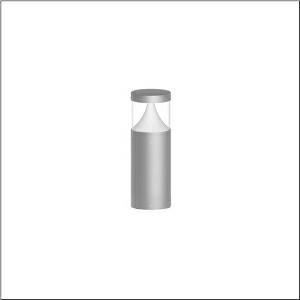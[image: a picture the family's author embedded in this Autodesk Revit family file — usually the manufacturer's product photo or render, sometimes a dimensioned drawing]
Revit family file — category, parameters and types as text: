
# Revit family: cl_31_poller_40_5cl424603
name_source: partatom
category: Lighting Fixtures
units: mm (PartAtom-declared; Revit-internal decimal feet)

## family parameters
Cut with Voids When Loaded = No
Host = Face
Light Source = No
Part Type = Normal
Room Calculation Point = No
Round Connector Dimension = Use Diameter
Shared = No

## types (1)
- --- (1 x LED, 800 lm, 7.2 W, 3000K)
    Apparent Load = 7 VA
    CIE Flux Codes = 19 66 88 92 100
    Color Rendering = 80
    Color Temperature = 3000K
    Default Elevation = 1800 mm
    Description = CL 31 Bollard 40, bollard luminaire, primary light control with lens, of PC, primary optical cover: cover panel, of PC, transparent, secondary light control with reflector, of PC, primary light characteristic: asymmetric, LED, rated luminous flux: 800lm, luminous efficacy: 110lm/W, light colour: 830, colour temperature: 3000K, control gear: DALI, with terminal, 5-pole, max. 2.5mm², mains connection: 220..240V, AC, 50/60Hz, rated input power: 7.2W, luminaire housing, of aluminium, powder-coated, Siteco® metallic grey, diameter: 170mm, height: 400mm, protection rating (complete): IP65, insulation class (complete): insulation class I (protective earthing), certification: CE, ENEC, impact resistance: IK10, permissible operating ambient temperature for outdoor applications: -20..+50°C, packaging unit: 1 piece
    Height = 200 mm  [stored 0.656168 ft]
    Lamp = 1 x LED
    Lamp Light Flux = 800 lm
    Lamp Power = 7.2 W
    Lamp count = 1
    Length = 170 mm  [stored 0.557743 ft]
    Luminous efficacy = 111 lm/W
    Manufacturer = Siteco
    ModVariant = No
    Model = 5CL424603
    Mounting Place = Floor
    Mounting Type = Freestanding
    Number of Poles = 1
    OnlyDefault = Yes
    Power Factor = 1
    Product Name = CL 31 Poller 40
    Product group = bollard luminaire
    ProductGroupID = 1304
    Protection Class = Protection class I
    Protection Degree = IP 65
    RLX_Detail_Level = 1
    RLX_Emergency_Light_Flux = 0 lm
    RLX_Emergency_Type = 0
    RLX_Emergency_Type_DB = No
    RlxData = <blob elided: 62325 chars, md5=652fc642>
    Socket = socket
    Standby Power = 0 W
    System Light Flux = 800 lm
    System Power = 7 W
    Type Comments = factory setting: luminous flux: 100 % | dim-lin: 254 | 182 mA
    Type Image = l_1006907.jpg
    URL = http://relux.com
    VarID = @adj_195310
    Voltage = 0 V
    Weight = 0.00 kg
    Width = 0 mm  [stored 0 ft]

note: [stored X ft] marks values corroborated as IEEE doubles in the binary element streams (Revit-internal decimal feet)

## geometry (parser evidence)
native form markers: Blend x4, Sweep x14
no freeform markers — native parametric forms only
